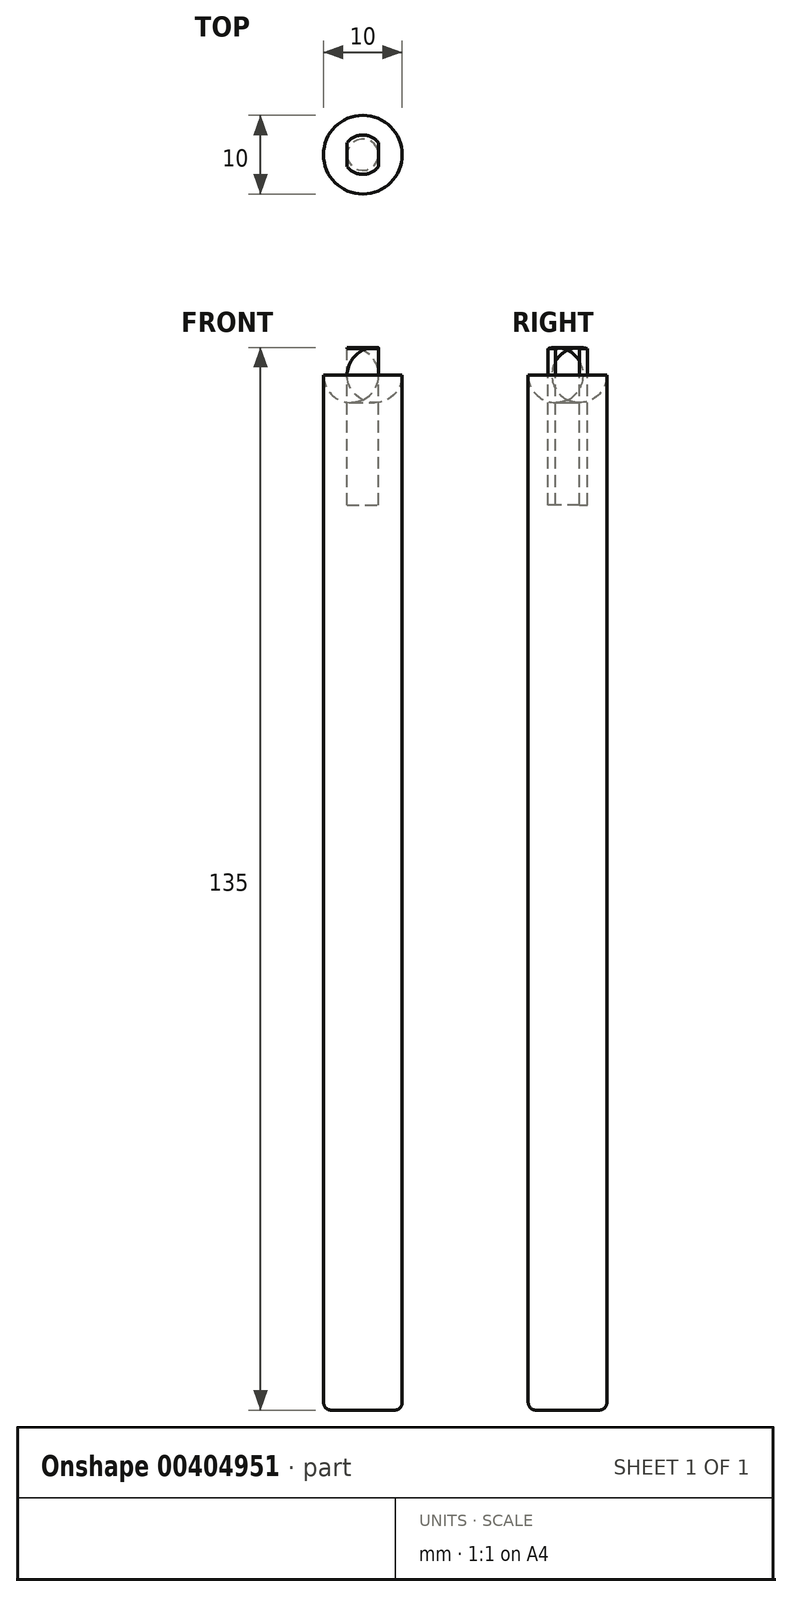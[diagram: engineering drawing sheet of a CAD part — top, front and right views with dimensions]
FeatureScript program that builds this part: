
annotation { "Feature Type Name" : "Feature", "Feature Type Description" : "" }
export const myFeature = defineFeature(function(context is Context, id is Id, definition is map)
    precondition{}
    {
        {
            var Q0;
            Q0=qCreatedBy(makeId("Right.planeOp"),FACE);
            var sketch = newSketch(context, id + "F0", { "sketchPlane" : qUnion([Q0])});
            skLineSegment(sketch, "E0", {"start": v(-5, 67.5) * mm, "end": v(0, 67.5) * mm});
            skLineSegment(sketch, "E1", {"start": v(0, 67.5) * mm, "end": v(0, -67.5) * mm});
            skLineSegment(sketch, "E2", {"start": v(0, -67.5) * mm, "end": v(-5, -67.5) * mm});
            skLineSegment(sketch, "E3", {"start": v(-5, 67.5) * mm, "end": v(-5, -67.5) * mm});
            skSolve(sketch);
        }
        {
            var Q0;
            Q0=makeQuery(id+"F0.imprint","IMPRINT",FACE,{"disambiguationData":[TD([[makeQuery(id+"F0.imprint","IMPRINT",EDGE,{"derivedFrom":sQuery(id+"F0.wireOp",EDGE,"E0")}),-1.0]])]});
            var Q1;
            Q1=sQuery(id+"F0.wireOp",EDGE,"E1");
            revolve(context, id + "F1", {"entities" : qUnion([Q0]), "axis" : qUnion([Q1]), "revolveType" : RevolveType.FULL});
        }
        {
            var Q0;
            Q0=makeQuery(id+"F1.opRevolve","SWEPT_FACE",FACE,{"disambiguationData":[OSD([sQuery(id+"F0.wireOp",EDGE,"E0")])]});
            var sketch = newSketch(context, id + "F2", { "sketchPlane" : qUnion([Q0])});
            skArc(sketch, "E4", {"start": v(-2, -1.5) * mm, "mid": v(0, -2.5) * mm, "end": v(2, -1.5) * mm});
            skLineSegment(sketch, "E5.left", {"start": v(-2, 1.5) * mm, "end": v(-2, -1.5) * mm});
            skLineSegment(sketch, "E5.right", {"start": v(2, 1.5) * mm, "end": v(2, -1.5) * mm});
            skArc(sketch, "E6.trimOffspring", {"start": v(2, 1.5) * mm, "mid": v(0, 2.5) * mm, "end": v(-2, 1.5) * mm});
            skSolve(sketch);
        }
        {
            var Q0;
            Q0=qSketchRegion(id+"F2",true);
            extrude(context, id + "F3", {"entities" : qUnion([Q0]), "operationType" : NewBodyOperationType.REMOVE, "oppositeDirection" : true, "depth" : 20 * mm});
        }
        {
            var Q0;
            Q0=makeQuery(id+"F1.opRevolve","SWEPT_EDGE",EDGE,{"disambiguationData":[OSD([sQuery(id+"F0.wireOp",EDGE,"E0"),sQuery(id+"F0.wireOp",EDGE,"E3")])]});
            fillet(context, id + "F4", {"entities" : qUnion([Q0]), "radius" : 3.5 * mm, "tangentPropagation" : true, "allowEdgeOverflow" : false});
        }
        {
            var Q0;
            Q0=makeQuery(id+"F1.opRevolve","SWEPT_EDGE",EDGE,{"disambiguationData":[OSD([sQuery(id+"F0.wireOp",EDGE,"E2"),sQuery(id+"F0.wireOp",EDGE,"E3")])]});
            fillet(context, id + "F5", {"entities" : qUnion([Q0]), "radius" : 1 * mm, "tangentPropagation" : true, "allowEdgeOverflow" : false});
        }
    });
